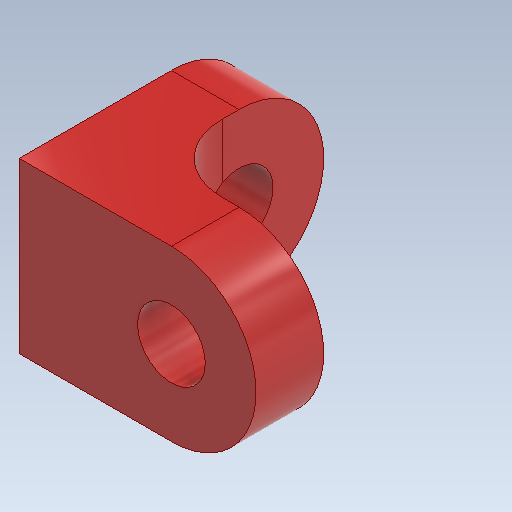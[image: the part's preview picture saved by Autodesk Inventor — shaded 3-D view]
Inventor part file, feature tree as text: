
AUTODESK INVENTOR PART (.ipt)
format: ipt  version: 2020 (Build 240168000, 168)  size: 139,264 bytes
history: native  units: mm
features: sketch x3, other x2
ambient origin geometry x8: Origin, YZ Plane, XZ Plane, XY Plane, X Axis, Y Axis, Z Axis, Center Point
bodies: Body1 (feature_tree)
feature tree (5):
  other  "OperaçãoIdentificador1"
  sketch  "Esboço1"  dims[d0=10.0mm]
  sketch  "Esboço2"
  sketch  "Esboço3"
  other  "Sólido1"
